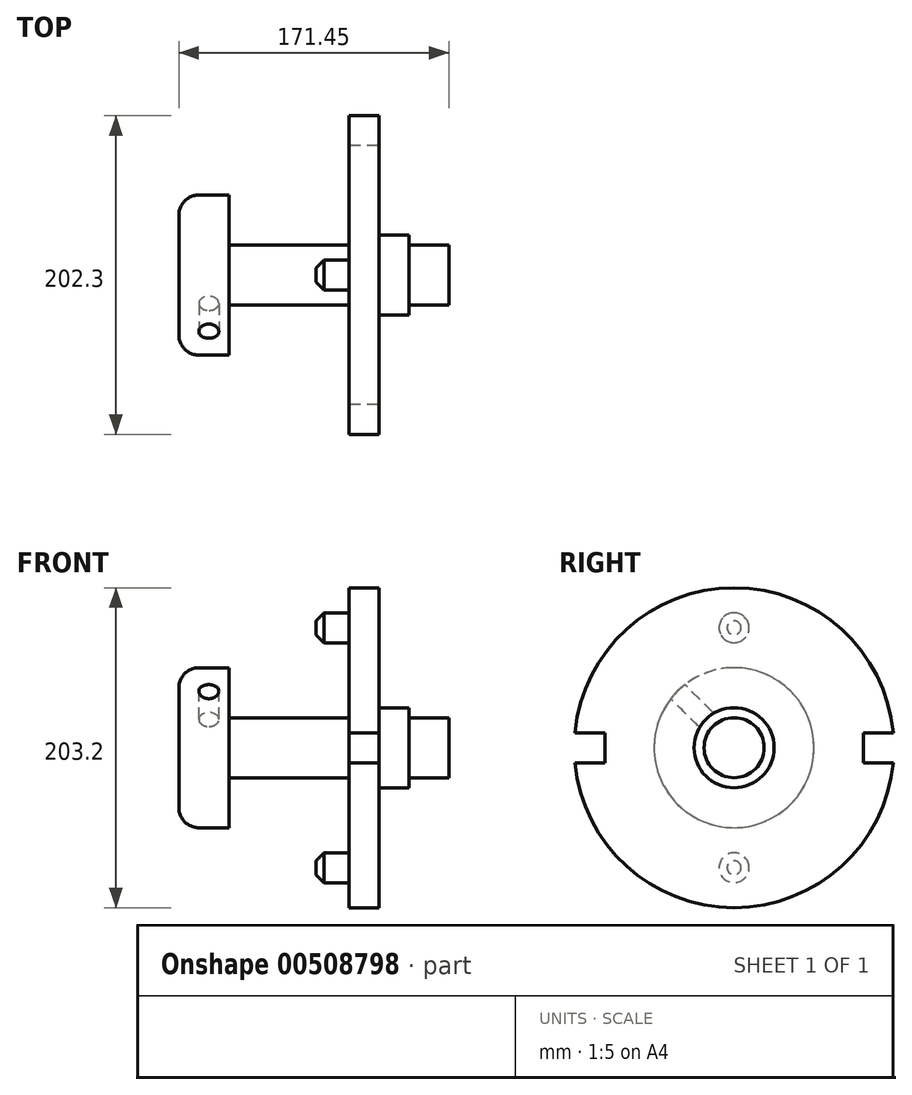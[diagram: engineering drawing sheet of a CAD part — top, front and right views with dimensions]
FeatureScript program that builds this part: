
annotation { "Feature Type Name" : "Feature", "Feature Type Description" : "" }
export const myFeature = defineFeature(function(context is Context, id is Id, definition is map)
    precondition{}
    {
        {
            var Q0;
            Q0=qCreatedBy(makeId("Front.planeOp"),FACE);
            var sketch = newSketch(context, id + "F0", { "sketchPlane" : qUnion([Q0])});
            skLineSegment(sketch, "E0", {"start": v(-314.96, 0) * mm, "end": v(248.68, 0) * mm, "construction": true});
            skLineSegment(sketch, "E1", {"start": v(0, 0) * mm, "end": v(0, 19.05) * mm});
            skLineSegment(sketch, "E2", {"start": v(0, 19.05) * mm, "end": v(-25.4, 19.05) * mm});
            skLineSegment(sketch, "E3", {"start": v(-25.4, 19.05) * mm, "end": v(-25.4, 25.4) * mm});
            skLineSegment(sketch, "E4", {"start": v(-25.4, 25.4) * mm, "end": v(-44.45, 25.4) * mm});
            skLineSegment(sketch, "E5", {"start": v(-44.45, 25.4) * mm, "end": v(-44.45, 101.6) * mm});
            skLineSegment(sketch, "E6", {"start": v(-44.45, 101.6) * mm, "end": v(-63.5, 101.6) * mm});
            skLineSegment(sketch, "E7", {"start": v(-63.5, 101.6) * mm, "end": v(-63.5, 19.05) * mm});
            skLineSegment(sketch, "E8", {"start": v(-63.5, 19.05) * mm, "end": v(-139.7, 19.05) * mm});
            skLineSegment(sketch, "E9", {"start": v(-139.7, 19.05) * mm, "end": v(-139.7, 50.8) * mm});
            skLineSegment(sketch, "E10", {"start": v(-139.7, 50.8) * mm, "end": v(-158.75, 50.8) * mm});
            skLineSegment(sketch, "E11", {"start": v(-171.45, 38.1) * mm, "end": v(-171.45, 0) * mm});
            skPoint(sketch, "E12.visualSharp", {"position": v(-171.45, 50.8) * mm});
            skArc(sketch, "E12.filletArc", {"start": v(-158.75, 50.8) * mm, "mid": v(-167.73, 47.08) * mm, "end": v(-171.45, 38.1) * mm});
            skLineSegment(sketch, "E13", {"start": v(-171.45, 0) * mm, "end": v(0, 0) * mm});
            skSolve(sketch);
        }
        {
            var Q0;
            Q0=makeQuery(id+"F0.imprint","IMPRINT",FACE,{"disambiguationData":[TD([[makeQuery(id+"F0.imprint","IMPRINT",EDGE,{"derivedFrom":sQuery(id+"F0.wireOp",EDGE,"E1")}),1.0]])]});
            var Q1;
            Q1=sQuery(id+"F0.wireOp",EDGE,"E0");
            revolve(context, id + "F1", {"entities" : qUnion([Q0]), "axis" : qUnion([Q1]), "revolveType" : RevolveType.FULL});
        }
        {
            var Q0;
            Q0=makeQuery(id+"F1.opRevolve","SWEPT_FACE",FACE,{"disambiguationData":[OSD([sQuery(id+"F0.wireOp",EDGE,"E7")])]});
            var sketch = newSketch(context, id + "F2", { "sketchPlane" : qUnion([Q0])});
            skLineSegment(sketch, "E14", {"start": v(0, 101.6) * mm, "end": v(0, -101.6) * mm, "construction": true});
            skCircle(sketch, "E15", {"center": v(0, 76.2) * mm, "radius": 9.53 * mm});
            skSolve(sketch);
        }
        {
            var Q0;
            Q0=makeQuery(id+"F2.imprint","IMPRINT",FACE,{"disambiguationData":[TD([[makeQuery(id+"F2.imprint","IMPRINT",EDGE,{"derivedFrom":sQuery(id+"F2.wireOp",EDGE,"E15")}),1.0]])]});
            extrude(context, id + "F3", {"entities" : qUnion([Q0]), "operationType" : NewBodyOperationType.ADD, "depth" : 20.83 * mm});
        }
        {
            var Q0;
            Q0=makeQuery(id+"F3.opExtrude","CAP_EDGE",EDGE,{"disambiguationData":[OSD([sQuery(id+"F2.wireOp",EDGE,"E15")])],"isStart":false});
            chamfer(context, id + "F4", {"entities" : qUnion([Q0]), "width" : 5.08 * mm, "tangentPropagation" : true});
        }
        {
            var Q0;
            Q0=makeQuery(id+"F1.opRevolve","SWEPT_FACE",FACE,{"disambiguationData":[OSD([sQuery(id+"F0.wireOp",EDGE,"E7")])]});
            var sketch = newSketch(context, id + "F5", { "sketchPlane" : qUnion([Q0])});
            skLineSegment(sketch, "E16", {"start": v(0, -101.6) * mm, "end": v(0, 0) * mm, "construction": true});
            skCircle(sketch, "E17", {"center": v(0, -76.2) * mm, "radius": 9.53 * mm});
            skSolve(sketch);
        }
        {
            var Q0;
            Q0=makeQuery(id+"F5.imprint","IMPRINT",FACE,{"disambiguationData":[TD([[makeQuery(id+"F5.imprint","IMPRINT",EDGE,{"derivedFrom":sQuery(id+"F5.wireOp",EDGE,"E17")}),1.0]])]});
            extrude(context, id + "F6", {"entities" : qUnion([Q0]), "depth" : 20.83 * mm});
        }
        {
            var Q0;
            Q0=makeQuery(id+"F6.opExtrude","CAP_EDGE",EDGE,{"disambiguationData":[OSD([sQuery(id+"F5.wireOp",EDGE,"E17")])],"isStart":false});
            chamfer(context, id + "F7", {"entities" : qUnion([Q0]), "width" : 5.08 * mm, "tangentPropagation" : true});
        }
        {
            var Q0;
            Q0=makeQuery(id+"F1.opRevolve","SWEPT_FACE",FACE,{"disambiguationData":[OSD([sQuery(id+"F0.wireOp",EDGE,"E7")])]});
            var sketch = newSketch(context, id + "F8", { "sketchPlane" : qUnion([Q0])});
            skLineSegment(sketch, "E18", {"start": v(-101.6, 0) * mm, "end": v(0, 0) * mm, "construction": true});
            skLineSegment(sketch, "E19", {"start": v(-101.15, 9.53) * mm, "end": v(-82.1, 9.53) * mm});
            skLineSegment(sketch, "E20", {"start": v(-82.1, 9.53) * mm, "end": v(-82.1, -9.53) * mm});
            skLineSegment(sketch, "E21", {"start": v(-82.1, -9.53) * mm, "end": v(-101.15, -9.53) * mm});
            skSolve(sketch);
        }
        {
            var Q0;
            {var subQ0=sQuery(id+"F8.wireOp",EDGE,"E19");Q0=makeQuery(id+"F8.imprint","IMPRINT",FACE,{"disambiguationData":[TD([[makeQuery(id+"F8.imprint","IMPRINT",EDGE,{"derivedFrom":subQ0}),-1.0]])]});}
            extrude(context, id + "F9", {"entities" : qUnion([Q0]), "operationType" : NewBodyOperationType.REMOVE, "oppositeDirection" : true, "depth" : 25.4 * mm});
        }
        {
            var Q0;
            Q0=makeQuery(id+"F1.opRevolve","SWEPT_FACE",FACE,{"disambiguationData":[OSD([sQuery(id+"F0.wireOp",EDGE,"E7")])]});
            var sketch = newSketch(context, id + "F10", { "sketchPlane" : qUnion([Q0])});
            skLineSegment(sketch, "E22", {"start": v(0, 0) * mm, "end": v(101.6, 0) * mm, "construction": true});
            skLineSegment(sketch, "E23", {"start": v(101.15, 9.53) * mm, "end": v(82.1, 9.53) * mm});
            skLineSegment(sketch, "E24", {"start": v(82.1, 9.53) * mm, "end": v(82.1, -9.52) * mm});
            skLineSegment(sketch, "E25", {"start": v(82.1, -9.52) * mm, "end": v(101.6, -9.52) * mm});
            skSolve(sketch);
        }
        {
            var Q0;
            {var subQ0=sQuery(id+"F10.wireOp",EDGE,"E23");Q0=makeQuery(id+"F10.imprint","IMPRINT",FACE,{"disambiguationData":[TD([[makeQuery(id+"F10.imprint","IMPRINT",EDGE,{"derivedFrom":subQ0}),1.0]])]});}
            extrude(context, id + "F11", {"entities" : qUnion([Q0]), "operationType" : NewBodyOperationType.REMOVE, "oppositeDirection" : true, "depth" : 25.4 * mm});
        }
        {
            var Q0;
            Q0=makeQuery(id+"F1.opRevolve","SWEPT_FACE",FACE,{"disambiguationData":[OSD([sQuery(id+"F0.wireOp",EDGE,"E9")])]});
            var sketch = newSketch(context, id + "F12", { "sketchPlane" : qUnion([Q0])});
            skLineSegment(sketch, "E26", {"start": v(0, 0) * mm, "end": v(-35.92, 35.92) * mm});
            skLineSegment(sketch, "E27", {"start": v(0, -64.38) * mm, "end": v(0, 24.9) * mm});
            skSolve(sketch);
        }
        {
            var Q0;
            Q0=sQuery(id+"F12.wireOp",VERTEX,"E26.end");
            var Q1;
            Q1=sQuery(id+"F12.wireOp",EDGE,"E26");
            cPlane(context, id + "F13", {"entities" : qUnion([Q0, Q1]), "cplaneType" : CPlaneType.LINE_POINT, "offset" : 25.4 * mm, "width" : 152.4 * mm, "height" : 152.4 * mm});
        }
        {
            var Q0;
            Q0=qCreatedBy(id+"F13.planeOp",FACE);
            var sketch = newSketch(context, id + "F14", { "sketchPlane" : qUnion([Q0])});
            skCircle(sketch, "E28", {"center": v(-152.4, 0) * mm, "radius": 6.35 * mm});
            skSolve(sketch);
        }
        {
            var Q0;
            Q0=makeQuery(id+"F14.imprint","IMPRINT",FACE,{"disambiguationData":[TD([[makeQuery(id+"F14.imprint","IMPRINT",EDGE,{"derivedFrom":sQuery(id+"F14.wireOp",EDGE,"E28")}),1.0]])]});
            extrude(context, id + "F15", {"entities" : qUnion([Q0]), "operationType" : NewBodyOperationType.REMOVE, "oppositeDirection" : true, "depth" : 25.4 * mm});
        }
    });
